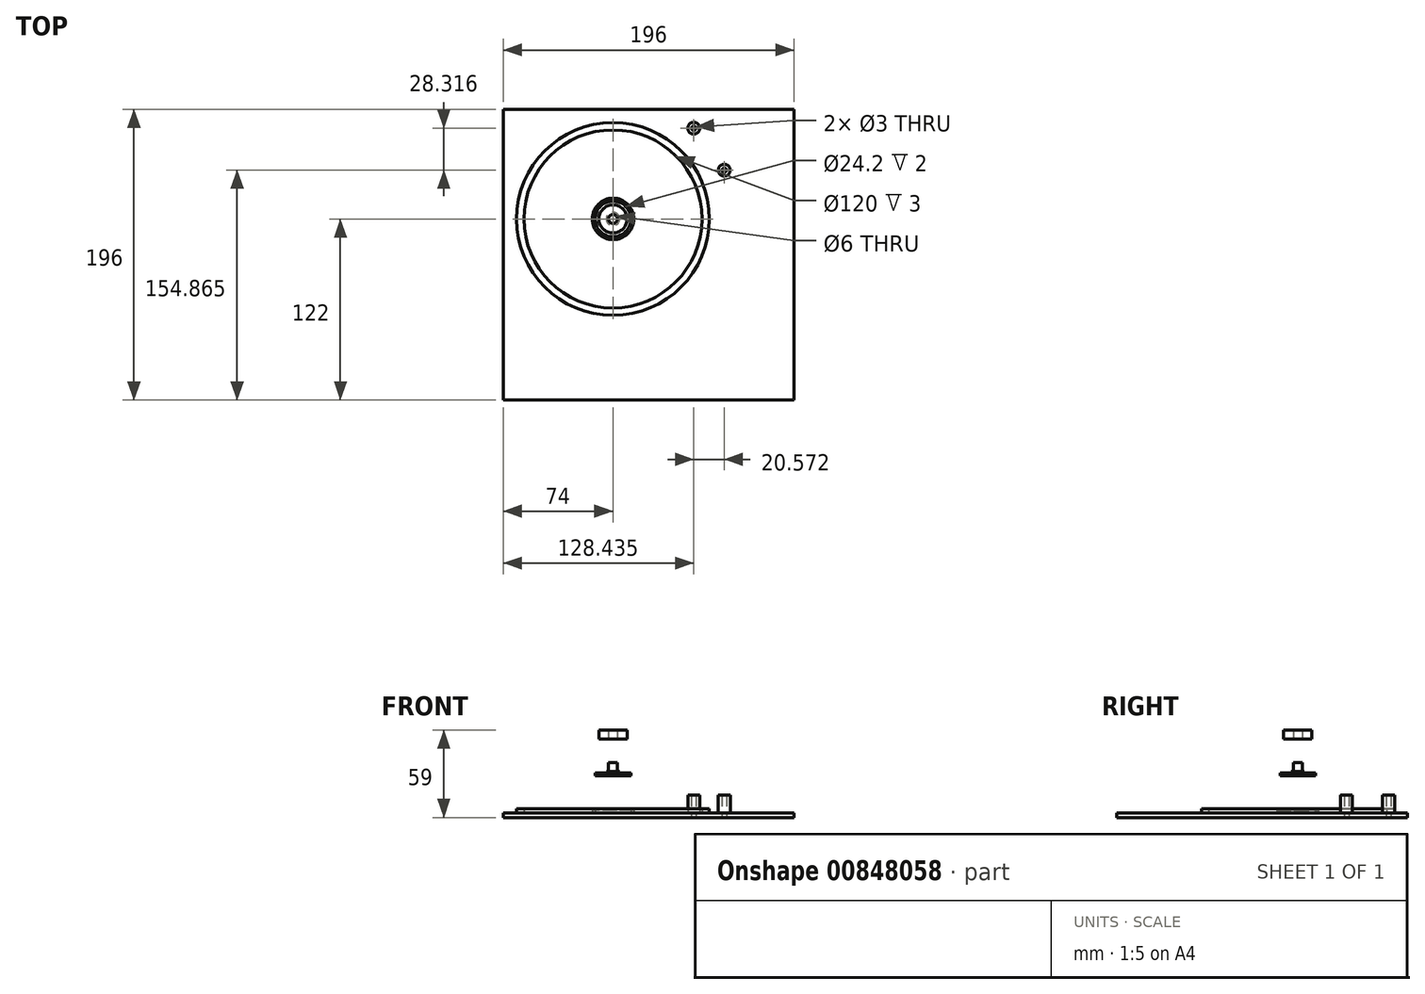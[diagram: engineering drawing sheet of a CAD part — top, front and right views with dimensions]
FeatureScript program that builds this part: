
annotation { "Feature Type Name" : "Feature", "Feature Type Description" : "" }
export const myFeature = defineFeature(function(context is Context, id is Id, definition is map)
    precondition{}
    {
        {
            var Q0;
            Q0=qCreatedBy(makeId("Top.planeOp"),FACE);
            var sketch = newSketch(context, id + "F0", { "sketchPlane" : qUnion([Q0])});
            skLineSegment(sketch, "E0.bottom", {"start": v(-98, 98) * mm, "end": v(98, 98) * mm});
            skLineSegment(sketch, "E0.top", {"start": v(-98, -98) * mm, "end": v(98, -98) * mm});
            skLineSegment(sketch, "E0.left", {"start": v(-98, 98) * mm, "end": v(-98, -98) * mm});
            skLineSegment(sketch, "E0.right", {"start": v(98, 98) * mm, "end": v(98, -98) * mm});
            skPoint(sketch, "E0.middle", {"position": v(0, 0) * mm});
            skLineSegment(sketch, "E1", {"start": v(-24, 98) * mm, "end": v(-24, -98) * mm, "construction": true});
            skLineSegment(sketch, "E2", {"start": v(-98, 24) * mm, "end": v(98, 24) * mm, "construction": true});
            skLineSegment(sketch, "E3.bottom", {"start": v(100, 100) * mm, "end": v(-100, 100) * mm, "construction": true});
            skLineSegment(sketch, "E3.top", {"start": v(100, -100) * mm, "end": v(-100, -100) * mm, "construction": true});
            skLineSegment(sketch, "E3.left", {"start": v(100, 100) * mm, "end": v(100, -100) * mm, "construction": true});
            skLineSegment(sketch, "E3.right", {"start": v(-100, 100) * mm, "end": v(-100, -100) * mm, "construction": true});
            skLineSegment(sketch, "E4", {"start": v(-24, 24) * mm, "end": v(77.85, 98) * mm, "construction": true});
            skCircle(sketch, "E5", {"center": v(34.25, 66.32) * mm, "radius": 2.5 * mm, "construction": true});
            skCircle(sketch, "E6", {"center": v(-24, 24) * mm, "radius": 65 * mm});
            skLineSegment(sketch, "E7", {"start": v(19.42, 86.73) * mm, "end": v(45.66, 50.62) * mm, "construction": true});
            skLineSegment(sketch, "E8", {"start": v(27.82, 88.78) * mm, "end": v(53.07, 54.03) * mm, "construction": true});
            skCircle(sketch, "E9", {"center": v(40.72, 71.02) * mm, "radius": 14 * mm, "construction": true});
            skCircle(sketch, "E10", {"center": v(30.44, 85.18) * mm, "radius": 1.5 * mm});
            skCircle(sketch, "E11", {"center": v(30.44, 85.18) * mm, "radius": 4 * mm});
            skCircle(sketch, "E12", {"center": v(51, 56.87) * mm, "radius": 1.5 * mm});
            skCircle(sketch, "E13", {"center": v(51, 56.87) * mm, "radius": 4 * mm});
            skCircle(sketch, "E14", {"center": v(-24, 24) * mm, "radius": 12.1 * mm});
            skCircle(sketch, "E15", {"center": v(-24, 24) * mm, "radius": 14 * mm});
            skCircle(sketch, "E16", {"center": v(-24, 24) * mm, "radius": 60 * mm});
            skLineSegment(sketch, "E17", {"start": v(-100, 100) * mm, "end": v(100, -100) * mm, "construction": true});
            skSolve(sketch);
        }
        {
            var Q0;
            Q0=makeQuery(id+"F0.imprint","IMPRINT",FACE,{"disambiguationData":[TD([[makeQuery(id+"F0.imprint","IMPRINT",EDGE,{"derivedFrom":sQuery(id+"F0.wireOp",EDGE,"E0.bottom")}),-1.0]])]});
            var Q1;
            Q1=makeQuery(id+"F0.imprint","IMPRINT",FACE,{"disambiguationData":[TD([[makeQuery(id+"F0.imprint","IMPRINT",EDGE,{"derivedFrom":sQuery(id+"F0.wireOp",EDGE,"E14")}),1.0]])]});
            var Q2;
            Q2=makeQuery(id+"F0.imprint","IMPRINT",FACE,{"disambiguationData":[TD([[makeQuery(id+"F0.imprint","IMPRINT",EDGE,{"derivedFrom":sQuery(id+"F0.wireOp",EDGE,"E14")}),-1.0]])]});
            var Q3;
            Q3=makeQuery(id+"F0.imprint","IMPRINT",FACE,{"disambiguationData":[TD([[makeQuery(id+"F0.imprint","IMPRINT",EDGE,{"derivedFrom":sQuery(id+"F0.wireOp",EDGE,"E15")}),-1.0]])]});
            var Q4;
            Q4=makeQuery(id+"F0.imprint","IMPRINT",FACE,{"disambiguationData":[TD([[makeQuery(id+"F0.imprint","IMPRINT",EDGE,{"derivedFrom":sQuery(id+"F0.wireOp",EDGE,"E6")}),1.0]])]});
            extrude(context, id + "F1", {"entities" : qUnion([Q0, Q1, Q2, Q3, Q4]), "depth" : 3 * mm, "offsetDistance" : 25 * mm});
        }
        {
            var Q0;
            Q0=makeQuery(id+"F0.imprint","IMPRINT",FACE,{"disambiguationData":[TD([[makeQuery(id+"F0.imprint","IMPRINT",EDGE,{"derivedFrom":sQuery(id+"F0.wireOp",EDGE,"E10")}),-1.0]])]});
            var Q1;
            Q1=makeQuery(id+"F0.imprint","IMPRINT",FACE,{"disambiguationData":[TD([[makeQuery(id+"F0.imprint","IMPRINT",EDGE,{"derivedFrom":sQuery(id+"F0.wireOp",EDGE,"E12")}),-1.0]])]});
            extrude(context, id + "F2", {"entities" : qUnion([Q0, Q1]), "operationType" : NewBodyOperationType.ADD, "depth" : 15 * mm, "offsetDistance" : 25 * mm});
        }
        {
            var Q0;
            Q0=makeQuery(id+"F1.opExtrude","CAP_FACE",FACE,{"disambiguationData":[OSD([sQuery(id+"F0.wireOp",EDGE,"E0.bottom"),sQuery(id+"F0.wireOp",EDGE,"E0.top"),sQuery(id+"F0.wireOp",EDGE,"E0.left"),sQuery(id+"F0.wireOp",EDGE,"E0.right"),sQuery(id+"F0.wireOp",EDGE,"0mZ89LyT-HtpB-klO3-zgrl-mv3TmblahrsZ")])],"isStart":false});
            cPlane(context, id + "F3", {"entities" : qUnion([Q0]), "cplaneType" : CPlaneType.OFFSET, "offset" : 25 * mm, "width" : 150 * mm, "height" : 150 * mm});
        }
        {
            var Q0;
            Q0=qCreatedBy(id+"F3.planeOp",FACE);
            var sketch = newSketch(context, id + "F4", { "sketchPlane" : qUnion([Q0])});
            skCircle(sketch, "E18", {"center": v(-24, 24) * mm, "radius": 12 * mm});
            skCircle(sketch, "E19", {"center": v(-24, 24) * mm, "radius": 4.5 * mm});
            skCircle(sketch, "E20", {"center": v(-24, 24) * mm, "radius": 3 * mm});
            skSolve(sketch);
        }
        {
            var Q0;
            Q0=makeQuery(id+"F4.imprint","IMPRINT",FACE,{"disambiguationData":[TD([[makeQuery(id+"F4.imprint","IMPRINT",EDGE,{"derivedFrom":sQuery(id+"F4.wireOp",EDGE,"E18")}),1.0]])]});
            extrude(context, id + "F5", {"entities" : qUnion([Q0]), "depth" : 2 * mm, "offsetDistance" : 25 * mm});
        }
        {
            var Q0;
            Q0=makeQuery(id+"F4.imprint","IMPRINT",FACE,{"disambiguationData":[TD([[makeQuery(id+"F4.imprint","IMPRINT",EDGE,{"derivedFrom":sQuery(id+"F4.wireOp",EDGE,"076896f3-0174-4496-88c8-60d10e4b6539.0")}),-1.0]])]});
            var Q1;
            Q1=makeQuery(id+"F4.imprint","IMPRINT",FACE,{"disambiguationData":[TD([[makeQuery(id+"F4.imprint","IMPRINT",EDGE,{"derivedFrom":sQuery(id+"F4.wireOp",EDGE,"E19")}),1.0]])]});
            extrude(context, id + "F6", {"entities" : qUnion([Q0, Q1]), "operationType" : NewBodyOperationType.ADD, "depth" : 3 * mm, "offsetDistance" : 25 * mm});
        }
        {
            var Q0;
            Q0=makeQuery(id+"F4.imprint","IMPRINT",FACE,{"disambiguationData":[TD([[makeQuery(id+"F4.imprint","IMPRINT",EDGE,{"derivedFrom":sQuery(id+"F4.wireOp",EDGE,"076896f3-0174-4496-88c8-60d10e4b6539.0")}),1.0]])]});
            var Q1;
            Q1=makeQuery(id+"F4.imprint","IMPRINT",FACE,{"disambiguationData":[TD([[makeQuery(id+"F4.imprint","IMPRINT",EDGE,{"derivedFrom":sQuery(id+"F4.wireOp",EDGE,"E20")}),1.0]])]});
            extrude(context, id + "F7", {"entities" : qUnion([Q0, Q1]), "operationType" : NewBodyOperationType.ADD, "depth" : 9 * mm, "offsetDistance" : 25 * mm});
        }
        {
            var Q0;
            Q0=makeQuery(id+"F0.imprint","IMPRINT",FACE,{"disambiguationData":[TD([[makeQuery(id+"F0.imprint","IMPRINT",EDGE,{"derivedFrom":sQuery(id+"F0.wireOp",EDGE,"E14")}),-1.0]])]});
            extrude(context, id + "F8", {"entities" : qUnion([Q0]), "operationType" : NewBodyOperationType.ADD, "depth" : 5 * mm, "offsetDistance" : 25 * mm});
        }
        {
            var Q0;
            Q0=qCreatedBy(id+"F3.planeOp",FACE);
            cPlane(context, id + "F9", {"entities" : qUnion([Q0]), "cplaneType" : CPlaneType.OFFSET, "offset" : 25 * mm, "width" : 150 * mm, "height" : 150 * mm});
        }
        {
            var Q0;
            Q0=qCreatedBy(id+"F9.planeOp",FACE);
            var sketch = newSketch(context, id + "F10", { "sketchPlane" : qUnion([Q0])});
            skPoint(sketch, "E21.0", {"position": v(-24, 24) * mm});
            skCircle(sketch, "E22", {"center": v(-24, 24) * mm, "radius": 3 * mm});
            skCircle(sketch, "E23", {"center": v(-24, 24) * mm, "radius": 9.5 * mm});
            skSolve(sketch);
        }
        {
            var Q0;
            Q0 = qSketchRegion(id + "F10", true);
            extrude(context, id + "F11", {"entities" : qUnion([Q0]), "depth" : 6 * mm, "offsetDistance" : 25 * mm});
        }
        {
            var Q0;
            Q0=makeQuery(id+"F0.imprint","IMPRINT",FACE,{"disambiguationData":[TD([[makeQuery(id+"F0.imprint","IMPRINT",EDGE,{"derivedFrom":sQuery(id+"F0.wireOp",EDGE,"E6")}),1.0]])]});
            extrude(context, id + "F12", {"entities" : qUnion([Q0]), "operationType" : NewBodyOperationType.ADD, "depth" : 6 * mm, "offsetDistance" : 25 * mm});
        }
    });
